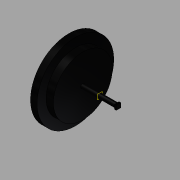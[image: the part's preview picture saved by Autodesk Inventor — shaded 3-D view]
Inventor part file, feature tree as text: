
AUTODESK INVENTOR PART (.ipt)
format: ipt  version: 2015 (Build 190159000, 159)  size: 141,312 bytes
history: native  units: in
note: dims shown in document units (in); Inventor stores cm internally (conversion verified against a paired STEP export)
features: sketch x5, other x3, plane x1
ambient origin geometry x8: Origin, YZ Plane, XZ Plane, XY Plane, X Axis, Y Axis, Z Axis, Center Point
bodies: Solid1 (feature_tree)
feature tree (9):
  other  "rueda_MIR4.ipt"
  other  "Solid1::rueda_MIR4.ipt"
  other  "TaggingFeature1"
  sketch  "Sketch2"  dims[d0=0.3937in]
  sketch  "Sketch3"
  sketch  "Sketch7"
  sketch  "Sketch12"
  sketch  "Sketch13"
  plane  "Work Plane1"
